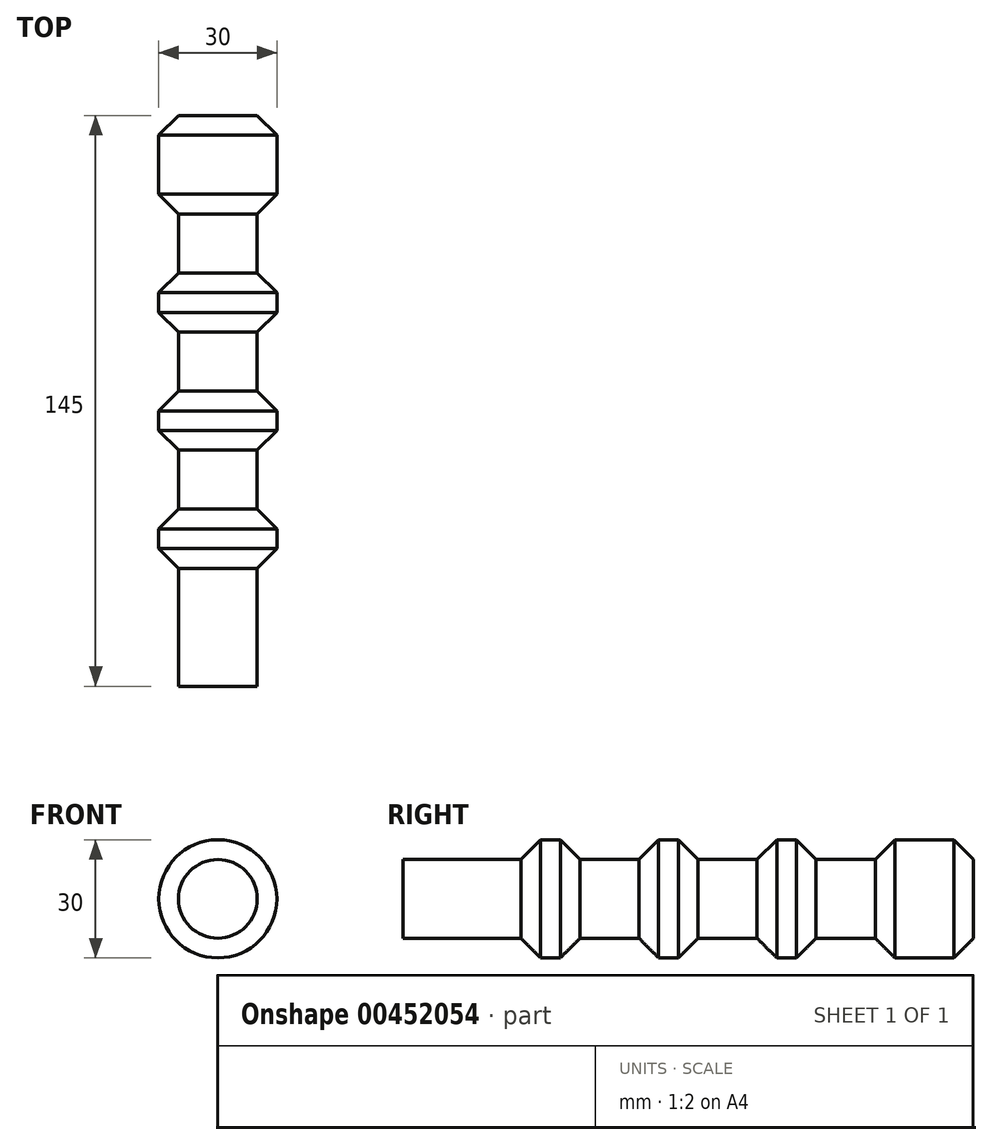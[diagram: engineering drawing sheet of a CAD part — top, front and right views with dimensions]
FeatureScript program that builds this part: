
annotation { "Feature Type Name" : "Feature", "Feature Type Description" : "" }
export const myFeature = defineFeature(function(context is Context, id is Id, definition is map)
    precondition{}
    {
        {
            var Q0;
            Q0=qCreatedBy(makeId("Top.planeOp"),FACE);
            var sketch = newSketch(context, id + "F0", { "sketchPlane" : qUnion([Q0])});
            skLineSegment(sketch, "E0", {"start": v(0, 0) * mm, "end": v(0, 145) * mm});
            skLineSegment(sketch, "E1", {"start": v(0, 0) * mm, "end": v(10, 0) * mm});
            skLineSegment(sketch, "E2", {"start": v(10, 0) * mm, "end": v(10, 30) * mm});
            skLineSegment(sketch, "E3", {"start": v(10, 30) * mm, "end": v(15, 30) * mm});
            skLineSegment(sketch, "E4", {"start": v(15, 30) * mm, "end": v(15, 45) * mm});
            skLineSegment(sketch, "E5", {"start": v(15, 45) * mm, "end": v(10, 45) * mm});
            skLineSegment(sketch, "E6", {"start": v(10, 45) * mm, "end": v(10, 60) * mm});
            skLineSegment(sketch, "E7", {"start": v(10, 60) * mm, "end": v(15, 60) * mm});
            skLineSegment(sketch, "E8", {"start": v(15, 60) * mm, "end": v(15, 75) * mm});
            skLineSegment(sketch, "E9", {"start": v(15, 75) * mm, "end": v(10, 75) * mm});
            skLineSegment(sketch, "E10", {"start": v(10, 75) * mm, "end": v(10, 90) * mm});
            skLineSegment(sketch, "E11", {"start": v(10, 90) * mm, "end": v(15, 90) * mm});
            skLineSegment(sketch, "E12", {"start": v(15, 90) * mm, "end": v(15, 105) * mm});
            skLineSegment(sketch, "E13", {"start": v(15, 105) * mm, "end": v(10, 105) * mm});
            skLineSegment(sketch, "E14", {"start": v(10, 105) * mm, "end": v(10, 120) * mm});
            skLineSegment(sketch, "E15", {"start": v(10, 120) * mm, "end": v(15, 120) * mm});
            skLineSegment(sketch, "E16", {"start": v(15, 120) * mm, "end": v(15, 145) * mm});
            skLineSegment(sketch, "E17", {"start": v(0, 145) * mm, "end": v(15, 145) * mm});
            skSolve(sketch);
        }
        {
            var Q0;
            Q0=makeQuery(id+"F0.imprint","IMPRINT",FACE,{"disambiguationData":[TD([[makeQuery(id+"F0.imprint","IMPRINT",EDGE,{"derivedFrom":sQuery(id+"F0.wireOp",EDGE,"E0")}),-1.0]])]});
            var Q1;
            Q1=sQuery(id+"F0.wireOp",EDGE,"E0");
            revolve(context, id + "F1", {"entities" : qUnion([Q0]), "axis" : qUnion([Q1]), "revolveType" : RevolveType.FULL});
        }
        {
            var Q0;
            Q0=makeQuery(id+"F1.opRevolve","SWEPT_EDGE",EDGE,{"disambiguationData":[OSD([sQuery(id+"F0.wireOp",EDGE,"OYE3Mpul-4MWe-nc4t-iA3G-Rg85FMBFwqbD"),sQuery(id+"F0.wireOp",EDGE,"CgxHtdeJ-4Uvk-Rzg8-ehHy-kMQ76oM8L1iQ")])]});
            var Q1;
            Q1=makeQuery(id+"F1.opRevolve","SWEPT_EDGE",EDGE,{"disambiguationData":[OSD([sQuery(id+"F0.wireOp",EDGE,"Sg91EUZK-3BSS-uReV-rnea-eHE3c1mNv2tN"),sQuery(id+"F0.wireOp",EDGE,"OYE3Mpul-4MWe-nc4t-iA3G-Rg85FMBFwqbD")])]});
            var Q2;
            Q2=makeQuery(id+"F1.opRevolve","SWEPT_EDGE",EDGE,{"disambiguationData":[OSD([sQuery(id+"F0.wireOp",EDGE,"E12"),sQuery(id+"F0.wireOp",EDGE,"E13")])]});
            var Q3;
            Q3=makeQuery(id+"F1.opRevolve","SWEPT_EDGE",EDGE,{"disambiguationData":[OSD([sQuery(id+"F0.wireOp",EDGE,"E11"),sQuery(id+"F0.wireOp",EDGE,"E12")])]});
            var Q4;
            Q4=makeQuery(id+"F1.opRevolve","SWEPT_EDGE",EDGE,{"disambiguationData":[OSD([sQuery(id+"F0.wireOp",EDGE,"E8"),sQuery(id+"F0.wireOp",EDGE,"E9")])]});
            var Q5;
            Q5=makeQuery(id+"F1.opRevolve","SWEPT_EDGE",EDGE,{"disambiguationData":[OSD([sQuery(id+"F0.wireOp",EDGE,"E7"),sQuery(id+"F0.wireOp",EDGE,"E8")])]});
            var Q6;
            Q6=makeQuery(id+"F1.opRevolve","SWEPT_EDGE",EDGE,{"disambiguationData":[OSD([sQuery(id+"F0.wireOp",EDGE,"E4"),sQuery(id+"F0.wireOp",EDGE,"E5")])]});
            var Q7;
            Q7=makeQuery(id+"F1.opRevolve","SWEPT_EDGE",EDGE,{"disambiguationData":[OSD([sQuery(id+"F0.wireOp",EDGE,"E3"),sQuery(id+"F0.wireOp",EDGE,"E4")])]});
            var Q8;
            Q8=makeQuery(id+"F1.opRevolve","SWEPT_EDGE",EDGE,{"disambiguationData":[OSD([sQuery(id+"F0.wireOp",EDGE,"E15"),sQuery(id+"F0.wireOp",EDGE,"E16")])]});
            var Q9;
            Q9=makeQuery(id+"F1.opRevolve","SWEPT_EDGE",EDGE,{"disambiguationData":[OSD([sQuery(id+"F0.wireOp",EDGE,"E16"),sQuery(id+"F0.wireOp",EDGE,"E17")])]});
            chamfer(context, id + "F2", {"entities" : qUnion([Q0, Q1, Q2, Q3, Q4, Q5, Q6, Q7, Q8, Q9]), "width" : 5 * mm, "tangentPropagation" : true});
        }
    });
